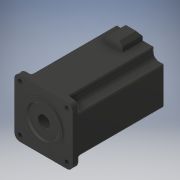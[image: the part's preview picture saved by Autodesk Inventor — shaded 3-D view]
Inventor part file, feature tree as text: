
AUTODESK INVENTOR PART (.ipt)
format: ipt  version: 2018 (Build 220112000, 112)  size: 387,072 bytes
history: native  units: mm
features: extrude x13, sketch x13, chamfer x5, projected_geometry x4, fillet x3, hole x1, plane x1
ambient origin geometry x8: Origin, YZ Plane, XZ Plane, XY Plane, X Axis, Y Axis, Z Axis, Center Point
bodies: Solid1 (feature_tree)
feature tree (40):
  extrude  "Extrusion1"  Depth=86.0mm
  extrude  "Extrusion2"  Depth=140.0mm
  extrude  "Extrusion3"  Depth=1.5mm
  hole  "Hole1"  [1 undecoded]
  plane  "Work Plane1"
  extrude  "Extrusion4"  Depth=13.0mm TaperAngle=0.0deg
  sketch  "Sketch6"  dims[d13=3.0mm d14=6.0mm d15=4.0mm d16=2.0mm d17=90.0deg d18=13.0mm d19=0.0mm d24=2.438mm d25=0.0mm]
  extrude  "Extrusion6"  Depth=69.6mm
  extrude  "Extrusion7"  Depth=120.0mm TaperAngle=0.0deg
  chamfer  "Chamfer1"  Distance=13.0mm
  fillet  "Fillet1"  Radius=8.0mm
  chamfer  "Chamfer2"  Distance=5.0mm Angle=45.0deg
  chamfer  "Chamfer3"  Distance=1.0mm Angle=45.0deg
  extrude  "Extrusion8"  Depth=56.0mm
  extrude  "Extrusion9"  Depth=3.0mm TaperAngle=45.0deg
  chamfer  "Chamfer4"  Distance=2.0mm
  fillet  "Fillet3"  Radius=15.0mm
  extrude  "Extrusion10"  Depth=15.0mm
  fillet  "Fillet4"  Radius=40.0mm
  extrude  "Extrusion11"  Depth=130.0mm TaperAngle=0.0deg
  chamfer  "Chamfer5"  Distance=2.0mm
  extrude  "Extrusion13"  Depth=8.0mm
  extrude  "Extrusion14"  Depth=2.0mm TaperAngle=0.0deg
  extrude  "Extrusion15"  Depth=2.0mm TaperAngle=45.0deg
  sketch  "Sketch1"  dims[d0=86.0mm d1=86.0mm]
  sketch  "Sketch2"  dims[d2=140.0mm d3=0.0mm d5=60.0mm]
  sketch  "Sketch3"  dims[d6=1.5mm d7=0.0mm d8=14.0mm]
  sketch  "Sketch5"  dims[d9=40.0mm d10=0.0mm d11=10.0mm d12=10.0mm]
  projected_geometry  "Projected Loop1"
  sketch  "Sketch7"  dims[d36=6.5mm d37=69.6mm]
  projected_geometry  "Projected Loop2"
  sketch  "Sketch8"  dims[d38=69.6mm d39=120.0mm d40=0.0mm]
  sketch  "Sketch9"  dims[d41=25.0mm]
  projected_geometry  "Projected Loop3"
  sketch  "Sketch10"  dims[d42=30.0mm]
  sketch  "Sketch11"  dims[d43=5.0mm d46=13.0mm d47=0.0mm]
  sketch  "Sketch13"  dims[d48=5.0mm d49=7.0mm d50=45.0deg d51=8.0mm d53=5.0mm d54=7.0mm d55=45.0deg d56=1.0mm d57=7.0mm d58=45.0deg]
  projected_geometry  "Projected Loop5"
  sketch  "Sketch14"  dims[d59=3.0mm d60=0.0mm d61=56.0mm]
  sketch  "Sketch15"  dims[d62=3.0mm d63=0.0mm d64=3.0mm d65=7.0mm d66=45.0deg d67=2.0mm d71=15.0mm d72=15.0mm d73=40.0mm d75=360.0deg d77=130.0mm d78=0.0mm d79=2.0mm d81=8.0mm d82=2.0mm d83=0.0mm d84=2.0mm d85=7.0mm d86=45.0deg d90=13.0mm d91=10.0mm d92=0.0mm d93=10.0mm d94=0.0mm d95=10.0mm d96=0.0mm]
note: 1 required parameter value undecoded (feature->parameter linkage not recoverable at this tier; creation-order binding heuristic only, values carry confidence <= 0.55)
